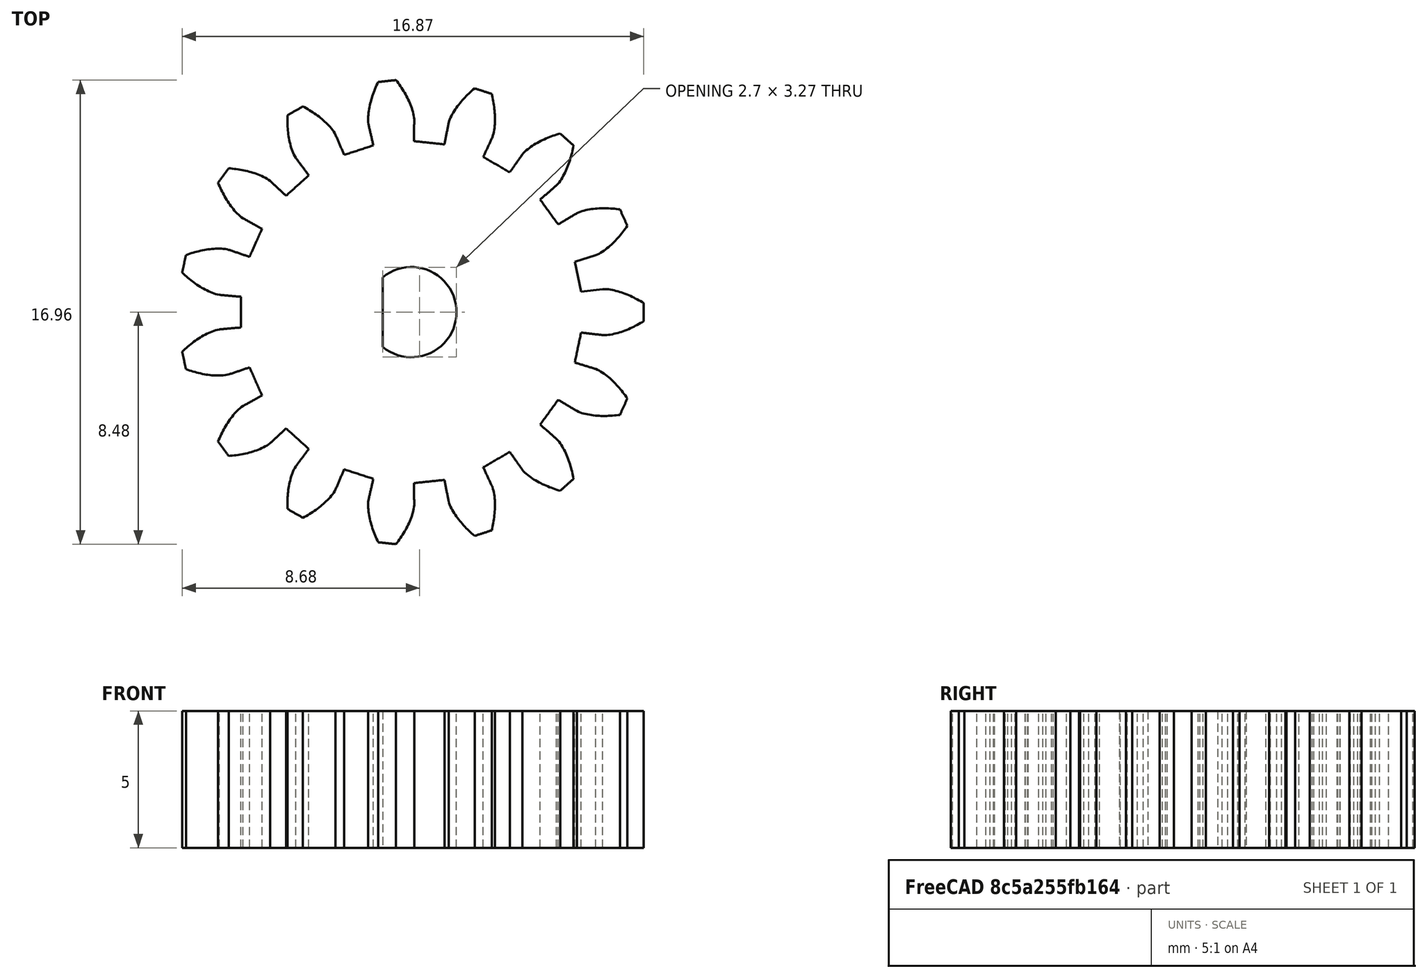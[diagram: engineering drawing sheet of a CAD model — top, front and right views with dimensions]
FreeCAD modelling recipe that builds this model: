
FCSTD DOCUMENT  (FreeCAD 0.20R29410 (Git))
Label: Gear
License: All rights reserved
LicenseURL: http://en.wikipedia.org/wiki/All_rights_reserved
objects: TechDraw::DrawViewDimension×5, TechDraw::DrawProjGroupItem×2, PartDesign::FeaturePython×1, Sketcher::SketchObject×1, PartDesign::Pocket×1, PartDesign::Body×1, TechDraw::DrawSVGTemplate×1, TechDraw::DrawProjGroup×1, TechDraw::DrawPage×1
note: 5 computed .brp shape members not serialized (recipe doc carries the construction recipe); baked Part::Feature solids carry a one-line shape summary decoded from their .brp

FEATURE [PartDesign::FeaturePython] InvoluteGear001  # WARN: FeaturePython — macro-defined, semantics opaque (R4)
  AttacherType = Attacher::AttachEngine3D
  angular_backlash = 0
  backlash = 0
  beta = 0
  clearance = 0.25
  da = 17
  df = 12.5
  double_helix = false
  dw = 15
  head = 0
  head_fillet = 0
  height = 5
  module = 1
  numpoints = 6
  pressure_angle = 20
  properties_from_tool = false
  reversed_backlash = false
  root_fillet = 0
  shift = 0
  simple = false
  teeth = 15
  transverse_pitch = 3.14159
  undercut = false
  version = 0.0.4
  expr: angular_backlash = backlash / dw * 360° / pi
  expr: dw = teeth * module
FEATURE [Sketcher::SketchObject] Sketch
  FullyConstrained = false
  MapMode = 5
  Placement = pos=(0,0,5) rot=(0,0,1;0rad)
  Support = -> [InvoluteGear001]
  sketch-geometry (4):
    g0: LineSegment StartX=-1.05 StartY=1.27279 StartZ=0 EndX=-1.05 EndY=-1.27279 EndZ=0
    g1: GeomPoint X=-1.65 Y=0 Z=0
    g2: ArcOfCircle CenterX=2.26e-14 CenterY=-1.69e-14 CenterZ=0 NormalX=0 NormalY=0 NormalZ=1 AngleXU=0 Radius=1.65 StartAngle=4.02261 EndAngle=8.54376
    g3: Circle CenterX=6.15175e-08 CenterY=0 CenterZ=0 NormalX=0 NormalY=0 NormalZ=1 AngleXU=0 Radius=1.65
  constraints (7):
    c: Parallel(g0,g-2)
    c: DistanceX(g1,g0) = 0.6
    c: PointOnObject(g1,g-1)
    c: PointOnObject(g1,g3)
    c: Diameter(g2) = 3.3
    c: Coincident(g0,g2)
    c: Coincident(g2,g0)
FEATURE [PartDesign::Pocket] Pocket
  BaseFeature = -> InvoluteGear001
  Direction = (0,0,-1)
  Length = 5
  Length2 = 5
  Profile = -> Sketch
  ReferenceAxis = -> Sketch [N_Axis]
  Type = 1
FEATURE [PartDesign::Body] Body  label="Gear"
  Group = -> [InvoluteGear001,Sketch,Pocket]
  Origin = -> Origin
  Tip = -> Pocket
FEATURE [TechDraw::DrawSVGTemplate] Template
  EditableTexts = Designed_by_Name=Белкин Никита; FC-Date=24.04.2023; FC-SC=4:1; FC-Title=Шестерня
  Height = 210
  Orientation = 1
  Width = 297
FEATURE [TechDraw::DrawProjGroupItem] ProjItem  label="Front"
  CoarseView = false
  Direction = (1,0,0)
  Focus = 100
  HardHidden = false
  IsoCount = 0
  IsoHidden = false
  IsoVisible = false
  LockPosition = true
  Perspective = false
  Rotation = 0
  RotationVector = (0,0,-1)
  Scale = 4
  ScaleType = 2
  SeamHidden = false
  SeamVisible = true
  SmoothHidden = false
  SmoothVisible = true
  Source = -> [Body]
  Type = 0
  X = 0
  XDirection = (0,0,-1)
  Y = 0
FEATURE [TechDraw::DrawProjGroupItem] ProjItem001  label="Left"
  CoarseView = false
  Direction = (1e-16,0,1)
  Focus = 100
  HardHidden = false
  IsoCount = 0
  IsoHidden = false
  IsoVisible = false
  LockPosition = false
  Perspective = false
  Rotation = 0
  RotationVector = (1,0,0)
  Scale = 4
  ScaleType = 2
  SeamHidden = false
  SeamVisible = true
  SmoothHidden = false
  SmoothVisible = true
  Source = -> [Body]
  Type = 1
  X = 82.4798
  XDirection = (1,0,-1e-16)
  Y = 0
FEATURE [TechDraw::DrawProjGroup] ProjGroup
  Anchor = -> ProjItem
  AutoDistribute = true
  LockPosition = false
  ProjectionType = 0
  Rotation = 0
  Scale = 4
  ScaleType = 2
  Source = -> [Body]
  Views = -> [ProjItem,ProjItem001]
  X = 100.432
  Y = 124.091
  spacingX = 15
  spacingY = 15
FEATURE [TechDraw::DrawViewDimension] Dimension002
  AngleOverride = false
  Arbitrary = false
  ArbitraryTolerances = false
  EqualTolerance = true
  ExtensionAngle = 0
  FormatSpec = ⌀%.2w
  FormatSpecOverTolerance = %+.2w
  FormatSpecUnderTolerance = %+.2w
  Inverted = false
  LineAngle = 0
  LockPosition = false
  MeasureType = 1
  OverTolerance = 0
  References2D = -> [ProjItem001]
  Rotation = 0
  ScaleType = 0
  TheoreticalExact = false
  Type = 5
  UnderTolerance = 0
  X = 6.74365
  Y = 18.6006
FEATURE [TechDraw::DrawViewDimension] Dimension003
  AngleOverride = false
  Arbitrary = false
  ArbitraryTolerances = false
  EqualTolerance = true
  ExtensionAngle = 0
  FormatSpec = %.2w
  FormatSpecOverTolerance = %+.2w
  FormatSpecUnderTolerance = %+.2w
  Inverted = false
  LineAngle = 0
  LockPosition = false
  MeasureType = 1
  OverTolerance = 0
  References2D = -> [ProjItem001]
  Rotation = 0
  ScaleType = 0
  TheoreticalExact = false
  Type = 2
  UnderTolerance = 0
  X = -16.7533
  Y = 1.4428
FEATURE [TechDraw::DrawViewDimension] Dimension004
  AngleOverride = false
  Arbitrary = false
  ArbitraryTolerances = false
  EqualTolerance = true
  ExtensionAngle = 0
  FormatSpec = ⌀%.2w
  FormatSpecOverTolerance = %+.2w
  FormatSpecUnderTolerance = %+.2w
  Inverted = false
  LineAngle = 0
  LockPosition = false
  MeasureType = 1
  OverTolerance = 0
  References2D = -> [ProjItem001]
  Rotation = 0
  ScaleType = 0
  TheoreticalExact = false
  Type = 5
  UnderTolerance = 0
  X = 35.659
  Y = -31.3367
FEATURE [TechDraw::DrawViewDimension] Dimension
  AngleOverride = false
  Arbitrary = false
  ArbitraryTolerances = false
  EqualTolerance = true
  ExtensionAngle = 0
  FormatSpec = ⌀%.2w
  FormatSpecOverTolerance = %+.2w
  FormatSpecUnderTolerance = %+.2w
  Inverted = false
  LineAngle = 0
  LockPosition = false
  MeasureType = 1
  OverTolerance = 0
  References2D = -> [ProjItem001]
  Rotation = 0
  ScaleType = 0
  TheoreticalExact = false
  Type = 5
  UnderTolerance = 0
  X = -8.46452
  Y = -44.4837
FEATURE [TechDraw::DrawViewDimension] Dimension005
  AngleOverride = false
  Arbitrary = false
  ArbitraryTolerances = false
  EqualTolerance = true
  ExtensionAngle = 0
  FormatSpec = %.2w
  FormatSpecOverTolerance = %+.2w
  FormatSpecUnderTolerance = %+.2w
  Inverted = false
  LineAngle = 0
  LockPosition = false
  MeasureType = 1
  OverTolerance = 0
  References2D = -> [ProjItem]
  Rotation = 0
  ScaleType = 0
  TheoreticalExact = false
  Type = 1
  UnderTolerance = 0
  X = -0.710227
  Y = -37.8046
FEATURE [TechDraw::DrawPage] Page
  KeepUpdated = true
  NextBalloonIndex = 1
  ProjectionType = 0
  Template = -> Template
  Views = -> [ProjGroup,Dimension002,Dimension003,Dimension004,Dimension,Dimension005]
